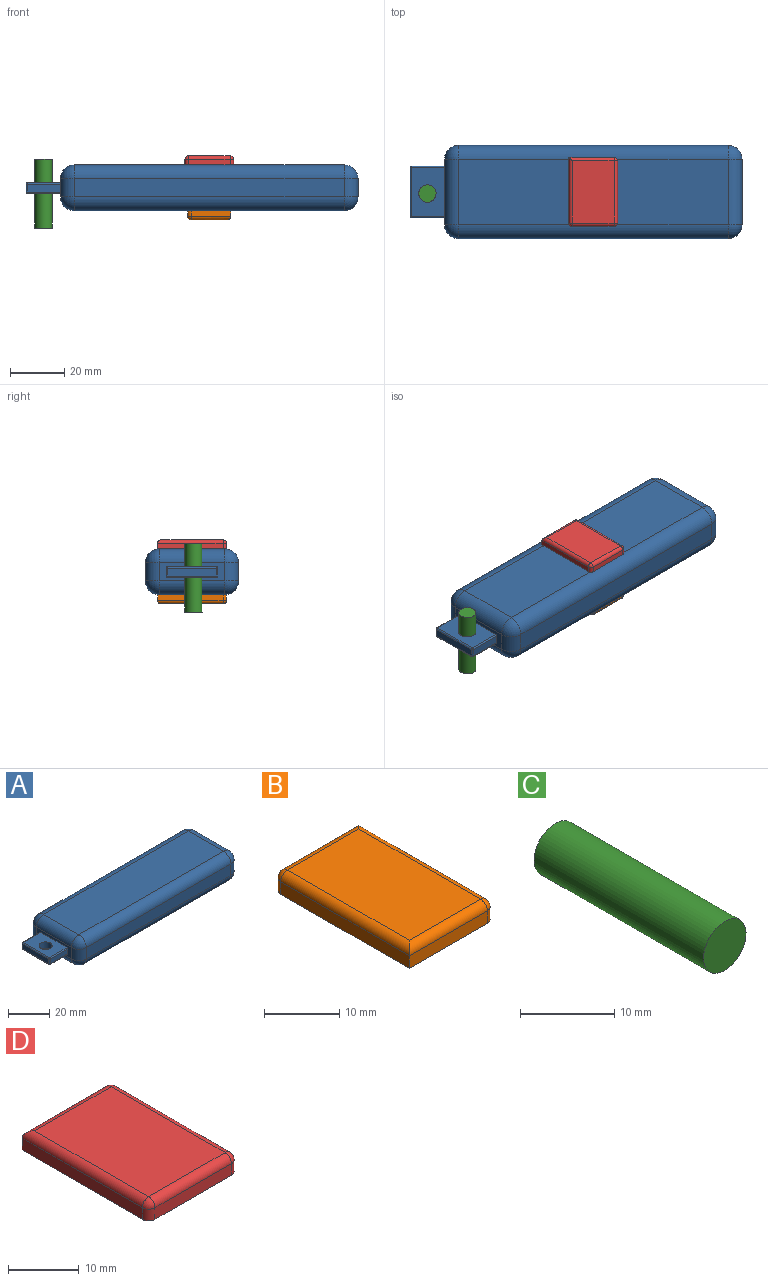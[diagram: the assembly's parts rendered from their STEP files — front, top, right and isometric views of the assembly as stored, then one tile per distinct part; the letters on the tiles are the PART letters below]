
ASSEMBLY  parts=4 mates=3
PART A: 44 faces, bbox 122.3x34.3x16.9 mm
  f0: plane 24.13x6.74mm, normal (-1,0,0), area 87.5mm2, adj f13,f15,f17,f21,f26,f27,f28,f29
  f1: plane 99.4x24.13mm, normal (0,0,-1), area 2398.6mm2, adj f7,f12,f17,f25
  f2: plane 24.13x6.74mm, normal (1,0,0), area 162.7mm2, adj f6,f7,f10,f22
  f3: plane 99.4x24.13mm, normal (0,0,1), area 2398.6mm2, adj f6,f8,f13,f18
  f4: plane 99.4x6.74mm, normal (0,-1,0), area 670mm2, adj f8,f10,f12,f15
  f5: plane 99.4x6.74mm, normal (0,1,0), area 670mm2, adj f18,f21,f22,f25
  f6: cylinder r=5.08mm len=24.13mm, axis (0,-1,0), area 192.5mm2, adj f2,f3,f9,f20
  f7: cylinder r=5.08mm len=24.13mm, axis (0,1,0), area 192.5mm2, adj f1,f2,f11,f24
  f8: cylinder r=5.08mm len=99.4mm, axis (1,0,0), area 793.2mm2, adj f3,f4,f9,f14
  f9: sphere r=5.08mm, area 40.5mm2, adj f6,f8,f10
  f10: cylinder r=5.08mm len=6.74mm, axis (0,0,-1), area 53.8mm2, adj f2,f4,f9,f11
  f11: sphere r=5.08mm, area 40.5mm2, adj f7,f10,f12
  f12: cylinder r=5.08mm len=99.4mm, axis (-1,0,0), area 793.2mm2, adj f1,f4,f11,f16
  f13: cylinder r=5.08mm len=24.13mm, axis (0,1,0), area 192.5mm2, adj f0,f3,f14,f19
  f14: sphere r=5.08mm, area 40.5mm2, adj f8,f13,f15
  f15: cylinder r=5.08mm len=6.74mm, axis (0,0,1), area 53.8mm2, adj f0,f4,f14,f16
  f16: sphere r=5.08mm, area 40.5mm2, adj f12,f15,f17
  f17: cylinder r=5.08mm len=24.13mm, axis (0,-1,0), area 192.5mm2, adj f0,f1,f16,f23
  f18: cylinder r=5.08mm len=99.4mm, axis (-1,0,0), area 793.2mm2, adj f3,f5,f19,f20
  f19: sphere r=5.08mm, area 40.5mm2, adj f13,f18,f21
  f20: sphere r=5.08mm, area 40.5mm2, adj f6,f18,f22
  f21: cylinder r=5.08mm len=6.74mm, axis (0,0,-1), area 53.8mm2, adj f0,f5,f19,f23
  f22: cylinder r=5.08mm len=6.74mm, axis (0,0,1), area 53.8mm2, adj f2,f5,f20,f24
  f23: sphere r=5.08mm, area 40.5mm2, adj f17,f21,f25
  f24: sphere r=5.08mm, area 40.5mm2, adj f7,f22,f25
  f25: cylinder r=5.08mm len=99.4mm, axis (1,0,0), area 793.2mm2, adj f1,f5,f23,f24
  f26: plane 12.19x2.93mm, normal (0,1,0), area 35.7mm2, adj f0,f32,f35,f36
  f27: plane 18.11x12.19mm, normal (0,0,-1), area 189.2mm2, adj f0,f33,f35,f41,f43
  f28: plane 12.19x2.93mm, normal (0,-1,0), area 35.7mm2, adj f0,f38,f40,f41
  f29: plane 18.11x12.19mm, normal (0,0,1), area 189.2mm2, adj f0,f31,f36,f38,f43
  f30: plane 18.11x2.93mm, normal (-1,0,0), area 53mm2, adj f31,f32,f33,f40
  f31: cylinder r=0.51mm len=18.11mm, axis (0,-1,0), area 14.5mm2, adj f29,f30,f37,f39
  f32: cylinder r=0.51mm len=2.93mm, axis (0,0,1), area 2.3mm2, adj f26,f30,f34,f37
  f33: cylinder r=0.51mm len=18.11mm, axis (0,1,0), area 14.5mm2, adj f27,f30,f34,f42
  f34: sphere r=0.51mm, area 0.4mm2, adj f32,f33,f35
  f35: cylinder r=0.51mm len=12.19mm, axis (-1,0,0), area 9.7mm2, adj f0,f26,f27,f34
  f36: cylinder r=0.51mm len=12.19mm, axis (1,0,0), area 9.7mm2, adj f0,f26,f29,f37
  f37: sphere r=0.51mm, area 0.4mm2, adj f31,f32,f36
  f38: cylinder r=0.51mm len=12.19mm, axis (-1,0,0), area 9.7mm2, adj f0,f28,f29,f39
  f39: sphere r=0.51mm, area 0.4mm2, adj f31,f38,f40
  f40: cylinder r=0.51mm len=2.93mm, axis (0,0,-1), area 2.3mm2, adj f28,f30,f39,f42
  f41: cylinder r=0.51mm len=12.19mm, axis (1,0,0), area 9.7mm2, adj f0,f27,f28,f42
  f42: sphere r=0.51mm, area 0.4mm2, adj f33,f40,f41
  f43: cylinder r=3.17mm len=6.35mm, axis (0,0,1), area 78.6mm2, adj f27,f29
PART B: 14 faces, bbox 15.9x25.4x3.3 mm
  f0: plane 24.13x2.03mm, normal (-1,0,0), area 49mm2, adj f1,f4,f7,f8
  f1: plane 25.4x15.93mm, normal (0,0,-1), area 403.9mm2, adj f0,f2,f4,f5,f8,f13
  f2: plane 24.13x2.03mm, normal (1,0,0), area 49mm2, adj f1,f5,f11,f13
  f3: plane 22.86x13.39mm, normal (0,0,1), area 306.1mm2, adj f6,f7,f10,f11
  f4: plane 14.66x2.03mm, normal (0,-1,0), area 29.8mm2, adj f0,f1,f6,f13
  f5: plane 14.66x2.03mm, normal (0,1,0), area 29.8mm2, adj f1,f2,f8,f10
  f6: cylinder r=1.27mm len=14.66mm, axis (1,0,0), area 28.3mm2, adj f3,f4,f7,f12
  f7: cylinder r=1.27mm len=24.13mm, axis (0,1,0), area 47.2mm2, adj f0,f3,f6,f9
  f8: cylinder r=1.27mm len=2.03mm, axis (0,0,-1), area 4.1mm2, adj f0,f1,f5,f9
  f9: sphere r=1.27mm, area 2.5mm2, adj f7,f8,f10
  f10: cylinder r=1.27mm len=14.66mm, axis (-1,0,0), area 28.3mm2, adj f3,f5,f9,f11
  f11: cylinder r=1.27mm len=24.13mm, axis (0,-1,0), area 47.2mm2, adj f2,f3,f10,f12
  f12: sphere r=1.27mm, area 2.5mm2, adj f6,f11,f13
  f13: cylinder r=1.27mm len=2.03mm, axis (0,0,-1), area 4.1mm2, adj f1,f2,f4,f12
PART C: 3 faces, bbox 6.4x25.4x6.4 mm
  f0: cylinder r=3.18mm len=25.4mm, axis (0,1,0), area 507.5mm2, adj f1,f2
  f1: plane 6.36x6.36mm, normal (0,-1,0), area 31.8mm2, adj f0
  f2: plane 6.36x6.36mm, normal (0,1,0), area 31.8mm2, adj f0
PART D: 16 faces, bbox 17.9x25.4x3.3 mm
  f0: plane 24.13x2.03mm, normal (-1,0,0), area 49mm2, adj f1,f5,f8,f10
  f1: plane 25.4x17.87mm, normal (0,0,-1), area 452.9mm2, adj f0,f2,f4,f5,f10,f11,f15
  f2: plane 22.86x2.03mm, normal (1,0,0), area 46.5mm2, adj f1,f11,f13,f15
  f3: plane 22.86x15.33mm, normal (0,0,1), area 350.5mm2, adj f6,f7,f8,f13
  f4: plane 15.33x2.03mm, normal (0,-1,0), area 31.2mm2, adj f1,f6,f10,f15
  f5: plane 16.6x2.03mm, normal (0,1,0), area 33.7mm2, adj f0,f1,f7,f11
  f6: cylinder r=1.27mm len=15.33mm, axis (-1,0,0), area 30.6mm2, adj f3,f4,f9,f14
  f7: cylinder r=1.27mm len=16.6mm, axis (-1,0,0), area 32.2mm2, adj f3,f5,f8,f12
  f8: cylinder r=1.27mm len=24.13mm, axis (0,1,0), area 47.2mm2, adj f0,f3,f7,f9
  f9: sphere r=1.27mm, area 2.5mm2, adj f6,f8,f10
  f10: cylinder r=1.27mm len=2.03mm, axis (0,0,1), area 4.1mm2, adj f0,f1,f4,f9
  f11: cylinder r=1.27mm len=2.03mm, axis (0,0,1), area 4.1mm2, adj f1,f2,f5,f12
  f12: sphere r=1.27mm, area 2.5mm2, adj f7,f11,f13
  f13: cylinder r=1.27mm len=22.86mm, axis (0,-1,0), area 45.6mm2, adj f2,f3,f12,f14
  f14: sphere r=1.27mm, area 2.5mm2, adj f6,f13,f15
  f15: cylinder r=1.27mm len=2.03mm, axis (0,0,-1), area 4.1mm2, adj f1,f2,f4,f14
PLACE A t=(-21.45,-7.24,-19.1)mm fixed
PLACE B rot(axis=(1,0,0),180deg) t=(10.22,-37.08,-19.1)mm
PLACE C rot(axis=(1,0,0),90deg) t=(-66.67,-19.54,-0.06)mm
PLACE D t=(22.07,-11.69,-2.2)mm
MATE fastened D.f1 <-> A.f3  axis (0,0,-1) through (-23.59,-24.38,-2.2)mm
MATE fastened B.f1 <-> A.f1  axis (0,0,1) through (-23.59,-24.38,-19.1)mm
MATE slider C.f0 <-> A.f43  axis (0,0,1) through (-84.65,-24.96,-25.46)mm
